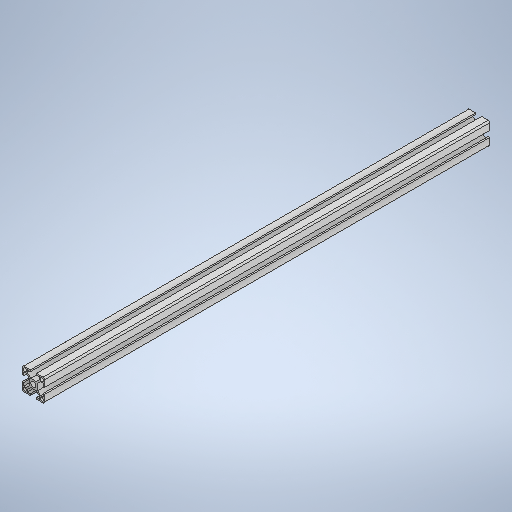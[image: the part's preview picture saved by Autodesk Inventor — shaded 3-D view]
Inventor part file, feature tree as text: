
AUTODESK INVENTOR PART (.ipt)
format: ipt  version: 2025 (Build 290162000, 162)  size: 315,392 bytes
history: native  units: in
note: dims shown in document units (in); Inventor stores cm internally (conversion verified against a paired STEP export)
features: extrude x1, sketch x1
ambient origin geometry x8: Origin, YZ Plane, XZ Plane, XY Plane, X Axis, Y Axis, Z Axis, Center Point
bodies: Solid1 (feature_tree)
feature tree (2):
  extrude  "Extrusion1"  Depth=23.622in
  sketch  "Sketch1"  dims[d6=23.622in d7=0.0in d8=0.1969in d9=0.0344in]
